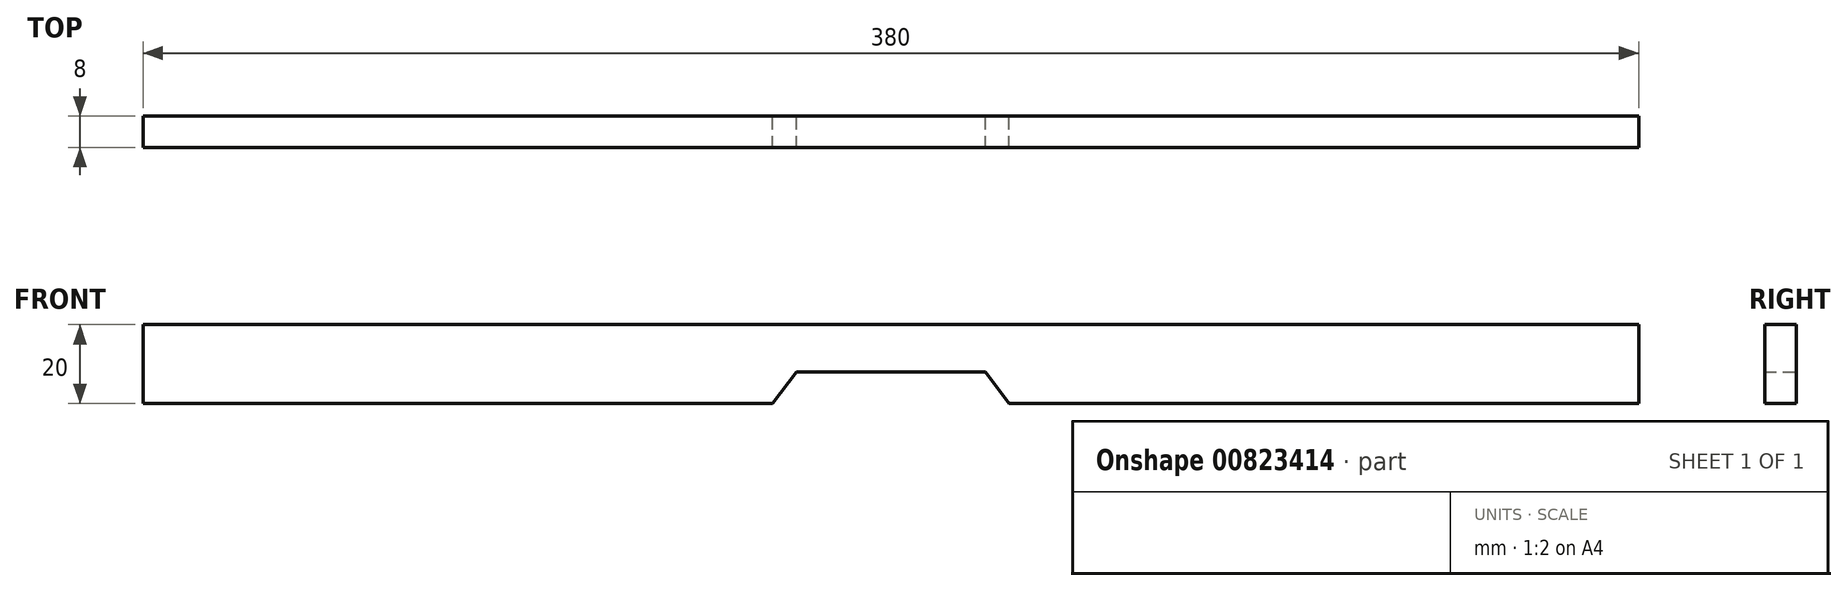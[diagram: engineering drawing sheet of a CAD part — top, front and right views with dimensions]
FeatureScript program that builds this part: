
annotation { "Feature Type Name" : "Feature", "Feature Type Description" : "" }
export const myFeature = defineFeature(function(context is Context, id is Id, definition is map)
    precondition{}
    {
        {
            var Q0;
            Q0=qCreatedBy(makeId("Front.planeOp"),FACE);
            var sketch = newSketch(context, id + "F0", { "sketchPlane" : qUnion([Q0])});
            skLineSegment(sketch, "E0.bottom", {"start": v(-190, 10) * mm, "end": v(190, 10) * mm});
            skLineSegment(sketch, "E0.top", {"start": v(-190, -10) * mm, "end": v(-30, -10) * mm});
            skLineSegment(sketch, "E0.left", {"start": v(-190, 10) * mm, "end": v(-190, -10) * mm});
            skLineSegment(sketch, "E0.right", {"start": v(190, 10) * mm, "end": v(190, -10) * mm});
            skPoint(sketch, "E0.middle", {"position": v(0, 0) * mm});
            skPoint(sketch, "E1", {"position": v(-30, -10) * mm});
            skPoint(sketch, "E2", {"position": v(30, -10) * mm});
            skPoint(sketch, "E3", {"position": v(-24, -2) * mm});
            skPoint(sketch, "E4", {"position": v(24, -2) * mm});
            skLineSegment(sketch, "E5", {"start": v(-30, -10) * mm, "end": v(-24, -2) * mm});
            skLineSegment(sketch, "E6", {"start": v(-24, -2) * mm, "end": v(24, -2) * mm});
            skLineSegment(sketch, "E7", {"start": v(24, -2) * mm, "end": v(30, -10) * mm});
            skLineSegment(sketch, "E8.trimOffspring", {"start": v(30, -10) * mm, "end": v(190, -10) * mm});
            skSolve(sketch);
        }
        {
            var Q0;
            Q0=makeQuery(id+"F0.imprint","IMPRINT",FACE,{"disambiguationData":[TD([[makeQuery(id+"F0.imprint","IMPRINT",EDGE,{"derivedFrom":sQuery(id+"F0.wireOp",EDGE,"E0.bottom")}),-1.0]])]});
            extrude(context, id + "F1", {"entities" : qUnion([Q0]), "depth" : 8 * mm, "offsetDistance" : 25 * mm});
        }
    });
